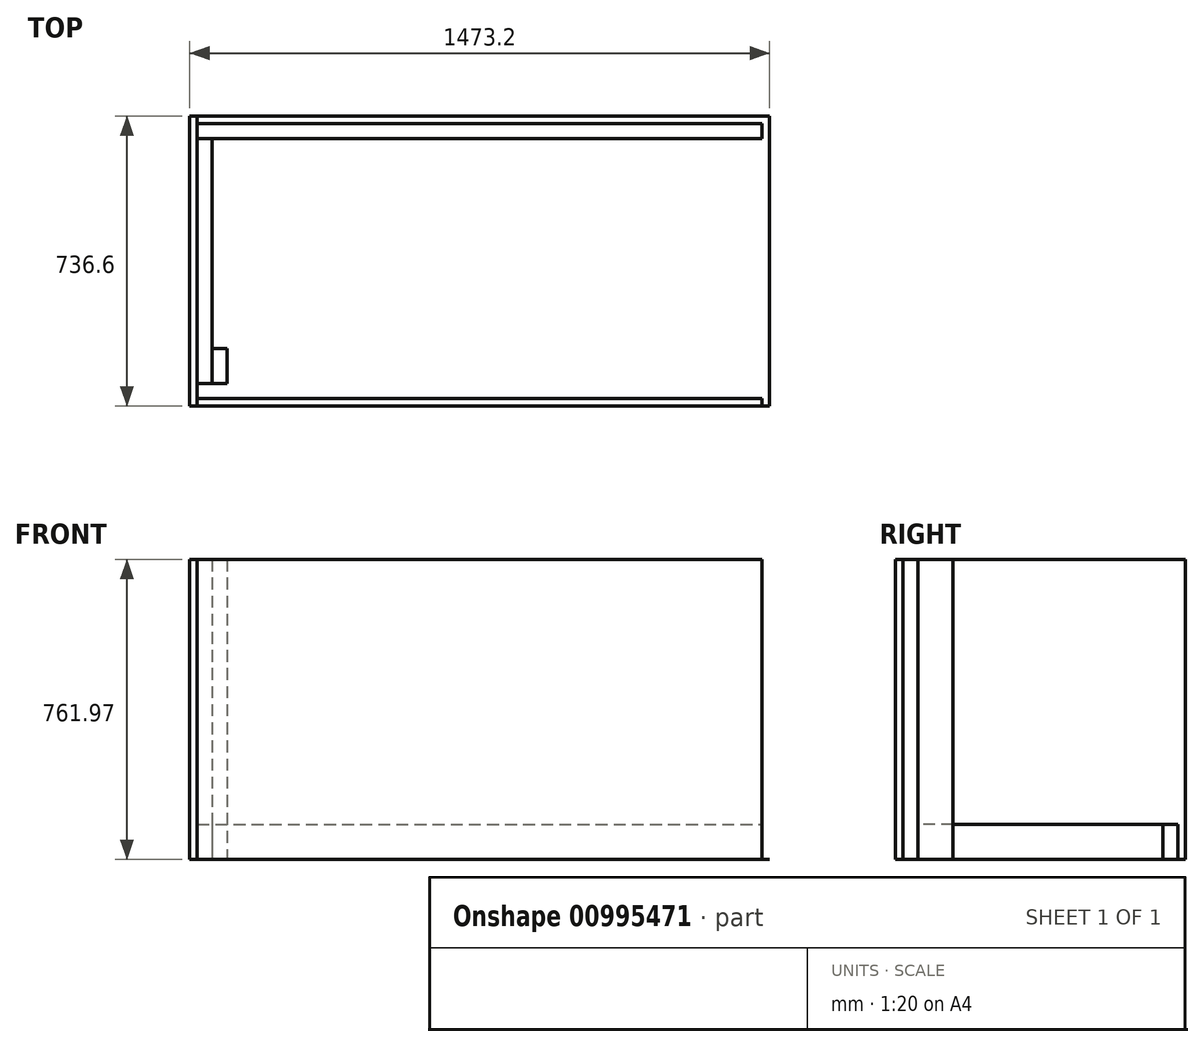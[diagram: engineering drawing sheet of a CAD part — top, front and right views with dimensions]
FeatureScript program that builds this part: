
annotation { "Feature Type Name" : "Feature", "Feature Type Description" : "" }
export const myFeature = defineFeature(function(context is Context, id is Id, definition is map)
    precondition{}
    {
        {
            assignVariable(context, id + "F0", {"name" : "sheetThickness", "anyValue" : 3 / 101.6 * mm});
        }
        {
            assignVariable(context, id + "F1", {"name" : "stockWidth", "anyValue" : 88.9 * mm});
        }
        {
            assignVariable(context, id + "F2", {"name" : "overallHeight", "anyValue" : 762 * mm});
        }
        {
            assignVariable(context, id + "F3", {"name" : "legLength", "anyValue" : getVariable(context, 'overallHeight') - getVariable(context, 'sheetThickness')});
        }
        {
            var Q0;
            Q0=qCreatedBy(makeId("Top.planeOp"),FACE);
            var sketch = newSketch(context, id + "F4", { "sketchPlane" : qUnion([Q0])});
            skLineSegment(sketch, "E0.bottom", {"start": v(736.6, -368.3) * mm, "end": v(-736.6, -368.3) * mm});
            skLineSegment(sketch, "E0.top", {"start": v(736.6, 368.3) * mm, "end": v(-736.6, 368.3) * mm});
            skLineSegment(sketch, "E0.left", {"start": v(736.6, -368.3) * mm, "end": v(736.6, 368.3) * mm});
            skLineSegment(sketch, "E0.right", {"start": v(-736.6, -368.3) * mm, "end": v(-736.6, 368.3) * mm});
            skPoint(sketch, "E0.middle", {"position": v(0, 0) * mm});
            skLineSegment(sketch, "E1.bottom", {"start": v(-736.6, 368.3) * mm, "end": v(736.6, 368.3) * mm});
            skSolve(sketch);
        }
        {
            var Q0;
            Q0=qCreatedBy(makeId("Top.planeOp"),FACE);
            var sketch = newSketch(context, id + "F5", { "sketchPlane" : qUnion([Q0])});
            skPoint(sketch, "E2.0", {"position": v(-736.6, 368.3) * mm});
            skPoint(sketch, "E3.0", {"position": v(736.6, 368.3) * mm});
            skPoint(sketch, "E4.0", {"position": v(-736.6, -368.3) * mm});
            skPoint(sketch, "E5.0", {"position": v(736.6, -368.3) * mm});
            skLineSegment(sketch, "E6.bottom", {"start": v(-736.6, 368.3) * mm, "end": v(-717.55, 368.3) * mm});
            skLineSegment(sketch, "E6.top", {"start": v(-736.6, -368.3) * mm, "end": v(-717.55, -368.3) * mm});
            skLineSegment(sketch, "E6.left", {"start": v(-736.6, 368.3) * mm, "end": v(-736.6, -368.3) * mm});
            skLineSegment(sketch, "E6.right", {"start": v(-717.55, 368.3) * mm, "end": v(-717.55, -368.3) * mm});
            skLineSegment(sketch, "E7.bottom", {"start": v(736.6, -368.3) * mm, "end": v(717.55, -368.3) * mm});
            skLineSegment(sketch, "E7.top", {"start": v(736.6, 368.3) * mm, "end": v(717.55, 368.3) * mm});
            skLineSegment(sketch, "E7.left", {"start": v(736.6, -368.3) * mm, "end": v(736.6, 368.3) * mm});
            skLineSegment(sketch, "E7.right", {"start": v(717.55, -368.3) * mm, "end": v(717.55, 368.3) * mm});
            skLineSegment(sketch, "E8.bottom", {"start": v(-717.55, -368.3) * mm, "end": v(717.55, -368.3) * mm});
            skLineSegment(sketch, "E8.top", {"start": v(-717.55, -349.25) * mm, "end": v(717.55, -349.25) * mm});
            skLineSegment(sketch, "E8.left", {"start": v(-717.55, -368.3) * mm, "end": v(-717.55, -349.25) * mm});
            skLineSegment(sketch, "E8.right", {"start": v(717.55, -368.3) * mm, "end": v(717.55, -349.25) * mm});
            skLineSegment(sketch, "E9.bottom", {"start": v(-717.55, 368.3) * mm, "end": v(717.55, 368.3) * mm});
            skLineSegment(sketch, "E9.top", {"start": v(-717.55, 349.25) * mm, "end": v(717.55, 349.25) * mm});
            skLineSegment(sketch, "E9.left", {"start": v(-717.55, 368.3) * mm, "end": v(-717.55, 349.25) * mm});
            skLineSegment(sketch, "E9.right", {"start": v(717.55, 368.3) * mm, "end": v(717.55, 349.25) * mm});
            skLineSegment(sketch, "E10", {"start": v(-717.55, 311.15) * mm, "end": v(717.55, 311.15) * mm});
            skLineSegment(sketch, "E11", {"start": v(-717.55, -311.15) * mm, "end": v(717.55, -311.15) * mm});
            skLineSegment(sketch, "E12", {"start": v(679.45, 311.15) * mm, "end": v(679.45, -311.15) * mm});
            skLineSegment(sketch, "E13", {"start": v(-679.45, 311.15) * mm, "end": v(-679.45, -311.15) * mm});
            skPoint(sketch, "E14", {"position": v(0, 311.15) * mm});
            skLineSegment(sketch, "E15.bottom", {"start": v(-19.05, 311.15) * mm, "end": v(-57.15, 311.15) * mm});
            skLineSegment(sketch, "E15.top", {"start": v(-19.05, -311.15) * mm, "end": v(-57.15, -311.15) * mm});
            skLineSegment(sketch, "E15.left", {"start": v(-19.05, 311.15) * mm, "end": v(-19.05, -311.15) * mm});
            skLineSegment(sketch, "E15.right", {"start": v(-57.15, 311.15) * mm, "end": v(-57.15, -311.15) * mm});
            skSolve(sketch);
        }
        {
            var Q0;
            Q0=qCreatedBy(makeId("Top.planeOp"),FACE);
            var sketch = newSketch(context, id + "F6", { "sketchPlane" : qUnion([Q0])});
            skPoint(sketch, "E16.0", {"position": v(-679.45, 311.15) * mm});
            skPoint(sketch, "E17.0", {"position": v(-679.45, -311.15) * mm});
            skPoint(sketch, "E18.0", {"position": v(679.45, 311.15) * mm});
            skPoint(sketch, "E19.0", {"position": v(679.45, -311.15) * mm});
            skLineSegment(sketch, "E20.bottom", {"start": v(-679.45, 311.15) * mm, "end": v(-641.35, 311.15) * mm});
            skLineSegment(sketch, "E20.top", {"start": v(-679.45, 222.25) * mm, "end": v(-641.35, 222.25) * mm});
            skLineSegment(sketch, "E20.left", {"start": v(-679.45, 311.15) * mm, "end": v(-679.45, 222.25) * mm});
            skLineSegment(sketch, "E20.right", {"start": v(-641.35, 311.15) * mm, "end": v(-641.35, 222.25) * mm});
            skLineSegment(sketch, "E21.bottom", {"start": v(-679.45, -311.15) * mm, "end": v(-641.35, -311.15) * mm});
            skLineSegment(sketch, "E21.top", {"start": v(-679.45, -222.25) * mm, "end": v(-641.35, -222.25) * mm});
            skLineSegment(sketch, "E21.left", {"start": v(-679.45, -311.15) * mm, "end": v(-679.45, -222.25) * mm});
            skLineSegment(sketch, "E21.right", {"start": v(-641.35, -311.15) * mm, "end": v(-641.35, -222.25) * mm});
            skLineSegment(sketch, "E22.bottom", {"start": v(679.45, 311.15) * mm, "end": v(641.35, 311.15) * mm});
            skLineSegment(sketch, "E22.top", {"start": v(679.45, 222.25) * mm, "end": v(641.35, 222.25) * mm});
            skLineSegment(sketch, "E22.left", {"start": v(679.45, 311.15) * mm, "end": v(679.45, 222.25) * mm});
            skLineSegment(sketch, "E22.right", {"start": v(641.35, 311.15) * mm, "end": v(641.35, 222.25) * mm});
            skLineSegment(sketch, "E23.bottom", {"start": v(679.45, -311.15) * mm, "end": v(641.35, -311.15) * mm});
            skLineSegment(sketch, "E23.top", {"start": v(679.45, -222.25) * mm, "end": v(641.35, -222.25) * mm});
            skLineSegment(sketch, "E23.left", {"start": v(679.45, -311.15) * mm, "end": v(679.45, -222.25) * mm});
            skLineSegment(sketch, "E23.right", {"start": v(641.35, -311.15) * mm, "end": v(641.35, -222.25) * mm});
            skPoint(sketch, "E24.0", {"position": v(-19.05, 311.15) * mm});
            skPoint(sketch, "E25.0", {"position": v(-19.05, -311.15) * mm});
            skLineSegment(sketch, "E26.bottom", {"start": v(-19.05, 311.15) * mm, "end": v(19.05, 311.15) * mm});
            skLineSegment(sketch, "E26.top", {"start": v(-19.05, 222.25) * mm, "end": v(19.05, 222.25) * mm});
            skLineSegment(sketch, "E26.left", {"start": v(-19.05, 311.15) * mm, "end": v(-19.05, 222.25) * mm});
            skLineSegment(sketch, "E26.right", {"start": v(19.05, 311.15) * mm, "end": v(19.05, 222.25) * mm});
            skLineSegment(sketch, "E27.bottom", {"start": v(-19.05, -311.15) * mm, "end": v(19.05, -311.15) * mm});
            skLineSegment(sketch, "E27.top", {"start": v(-19.05, -222.25) * mm, "end": v(19.05, -222.25) * mm});
            skLineSegment(sketch, "E27.left", {"start": v(-19.05, -311.15) * mm, "end": v(-19.05, -222.25) * mm});
            skLineSegment(sketch, "E27.right", {"start": v(19.05, -311.15) * mm, "end": v(19.05, -222.25) * mm});
            skSolve(sketch);
        }
        {
            var Q0;
            Q0=makeQuery(id+"F4.imprint","IMPRINT",FACE,{"disambiguationData":[TD([[makeQuery(id+"F4.imprint","IMPRINT",EDGE,{"derivedFrom":sQuery(id+"F4.wireOp",EDGE,"E0.bottom")}),-1.0]])]});
            extrude(context, id + "F7", {"entities" : qUnion([Q0]), "depth" : getVariable(context, 'sheetThickness'), "offsetDistance" : 25.4 * mm});
        }
        {
            var Q0;
            Q0=makeQuery(id+"F5.imprint","IMPRINT",FACE,{"disambiguationData":[TD([[makeQuery(id+"F5.imprint","IMPRINT",EDGE,{"derivedFrom":sQuery(id+"F5.wireOp",EDGE,"E6.bottom")}),-1.0]])]});
            extrude(context, id + "F8", {"entities" : qUnion([Q0]), "depth" : getVariable(context, 'legLength'), "offsetDistance" : 25.4 * mm});
        }
        {
            var Q0;
            Q0=makeQuery(id+"F5.imprint","IMPRINT",FACE,{"disambiguationData":[TD([[makeQuery(id+"F5.imprint","IMPRINT",EDGE,{"derivedFrom":sQuery(id+"F5.wireOp",EDGE,"E8.bottom")}),1.0]])]});
            extrude(context, id + "F9", {"entities" : qUnion([Q0]), "depth" : getVariable(context, 'legLength'), "offsetDistance" : 25.4 * mm});
        }
        {
            var Q0;
            {var subQ4=sQuery(id+"F5.wireOp",EDGE,"E9.top");Q0=makeQuery(id+"F5.imprint","IMPRINT",FACE,{"disambiguationData":[TD([[makeQuery(id+"F5.imprint","IMPRINT",EDGE,{"derivedFrom":subQ4}),-1.0]])]});}
            extrude(context, id + "F10", {"entities" : qUnion([Q0]), "depth" : getVariable(context, 'stockWidth'), "offsetDistance" : 25.4 * mm});
        }
        {
            var Q0;
            {var subQ5=sQuery(id+"F5.wireOp",EDGE,"E13");Q0=makeQuery(id+"F5.imprint","IMPRINT",FACE,{"disambiguationData":[TD([[makeQuery(id+"F5.imprint","IMPRINT",EDGE,{"derivedFrom":subQ5}),-1.0]])]});}
            extrude(context, id + "F11", {"entities" : qUnion([Q0]), "depth" : getVariable(context, 'stockWidth'), "offsetDistance" : 25.4 * mm});
        }
        {
            var Q0;
            Q0=makeQuery(id+"F6.imprint","IMPRINT",FACE,{"disambiguationData":[TD([[makeQuery(id+"F6.imprint","IMPRINT",EDGE,{"derivedFrom":sQuery(id+"F6.wireOp",EDGE,"E21.bottom")}),1.0]])]});
            extrude(context, id + "F12", {"entities" : qUnion([Q0]), "depth" : getVariable(context, 'legLength'), "offsetDistance" : 25.4 * mm});
        }
    });
